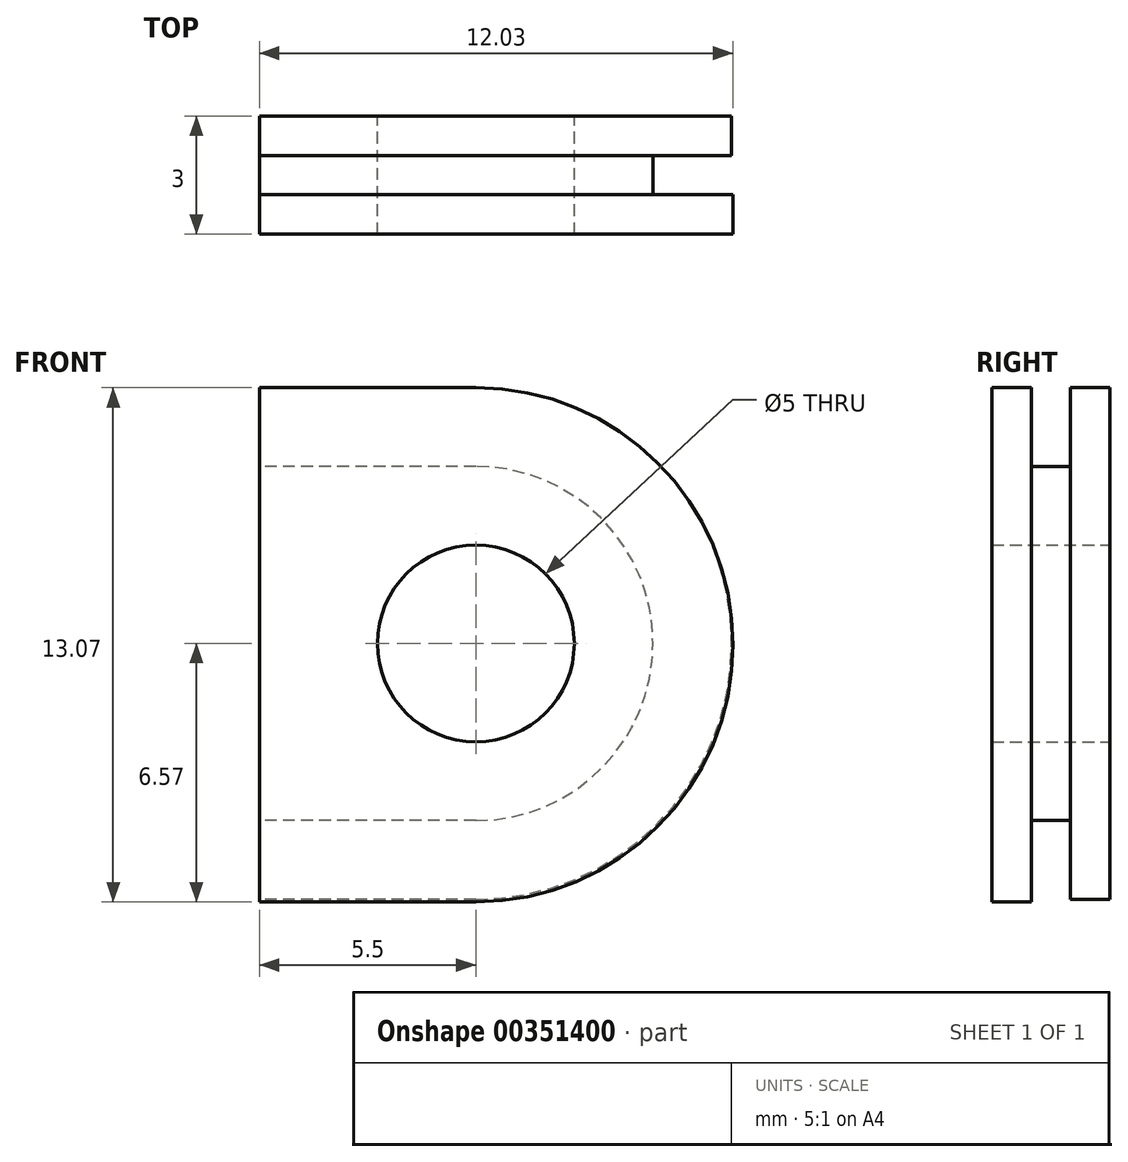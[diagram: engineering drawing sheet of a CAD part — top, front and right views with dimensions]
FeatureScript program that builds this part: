
annotation { "Feature Type Name" : "Feature", "Feature Type Description" : "" }
export const myFeature = defineFeature(function(context is Context, id is Id, definition is map)
    precondition{}
    {
        {
            var Q0;
            Q0=qCreatedBy(makeId("Front.planeOp"),FACE);
            var sketch = newSketch(context, id + "F0", { "sketchPlane" : qUnion([Q0])});
            skCircle(sketch, "E0", {"center": v(0, 0) * mm, "radius": 2.5 * mm});
            skLineSegment(sketch, "E1.bottom", {"start": v(0, 4.5) * mm, "end": v(-5.5, 4.5) * mm});
            skLineSegment(sketch, "E1.top", {"start": v(0, -4.5) * mm, "end": v(-5.5, -4.5) * mm});
            skLineSegment(sketch, "E1.left", {"start": v(0, 4.5) * mm, "end": v(0, -4.5) * mm});
            skLineSegment(sketch, "E1.right", {"start": v(-5.5, 4.5) * mm, "end": v(-5.5, -4.5) * mm});
            skArc(sketch, "E2", {"start": v(0, -4.5) * mm, "mid": v(4.5, 0) * mm, "end": v(0, 4.5) * mm});
            skSolve(sketch);
        }
        {
            var Q0;
            Q0 = qSketchRegion(id + "F0", true);
            extrude(context, id + "F1", {"entities" : qUnion([Q0]), "depth" : 1 * mm});
        }
        {
            var Q0;
            Q0=makeQuery(id+"F1.opExtrude","CAP_FACE",FACE,{"disambiguationData":[OSD([sQuery(id+"F0.wireOp",EDGE,"E0"),sQuery(id+"F0.wireOp",EDGE,"E1.bottom"),sQuery(id+"F0.wireOp",EDGE,"E1.top"),sQuery(id+"F0.wireOp",EDGE,"E1.right"),sQuery(id+"F0.wireOp",EDGE,"E2")])],"isStart":false});
            var sketch = newSketch(context, id + "F2", { "sketchPlane" : qUnion([Q0])});
            skLineSegment(sketch, "E3.bottom", {"start": v(0, 6.5) * mm, "end": v(-5.5, 6.5) * mm});
            skLineSegment(sketch, "E3.top", {"start": v(0, -6.57) * mm, "end": v(-5.5, -6.57) * mm});
            skLineSegment(sketch, "E3.left", {"start": v(0, 6.5) * mm, "end": v(0, -6.57) * mm});
            skLineSegment(sketch, "E3.right", {"start": v(-5.5, 6.5) * mm, "end": v(-5.5, -6.57) * mm});
            skCircle(sketch, "E4", {"center": v(0, 0) * mm, "radius": 2.5 * mm});
            skArc(sketch, "E5", {"start": v(0, -6.57) * mm, "mid": v(6.53, -0.03) * mm, "end": v(0, 6.5) * mm});
            skSolve(sketch);
        }
        {
            var Q0;
            Q0 = qSketchRegion(id + "F2", true);
            extrude(context, id + "F3", {"entities" : qUnion([Q0]), "operationType" : NewBodyOperationType.ADD, "depth" : 1 * mm});
        }
        {
            var Q0;
            Q0=makeQuery(id+"F1.opExtrude","CAP_FACE",FACE,{"disambiguationData":[OSD([sQuery(id+"F0.wireOp",EDGE,"E0"),sQuery(id+"F0.wireOp",EDGE,"E1.bottom"),sQuery(id+"F0.wireOp",EDGE,"E1.top"),sQuery(id+"F0.wireOp",EDGE,"E1.right"),sQuery(id+"F0.wireOp",EDGE,"E2")])],"isStart":true});
            var sketch = newSketch(context, id + "F4", { "sketchPlane" : qUnion([Q0])});
            skCircle(sketch, "E6", {"center": v(0, 0) * mm, "radius": 2.5 * mm});
            skLineSegment(sketch, "E7.bottom", {"start": v(0, 6.5) * mm, "end": v(5.5, 6.5) * mm});
            skLineSegment(sketch, "E7.top", {"start": v(0, -6.5) * mm, "end": v(5.5, -6.5) * mm});
            skLineSegment(sketch, "E7.left", {"start": v(0, 6.5) * mm, "end": v(0, -6.5) * mm});
            skLineSegment(sketch, "E7.right", {"start": v(5.5, 6.5) * mm, "end": v(5.5, -6.5) * mm});
            skArc(sketch, "E8", {"start": v(0, 6.5) * mm, "mid": v(-6.5, 0) * mm, "end": v(0, -6.5) * mm});
            skSolve(sketch);
        }
        {
            var Q0;
            Q0 = qSketchRegion(id + "F4", true);
            extrude(context, id + "F5", {"entities" : qUnion([Q0]), "operationType" : NewBodyOperationType.ADD, "depth" : 1 * mm});
        }
    });
